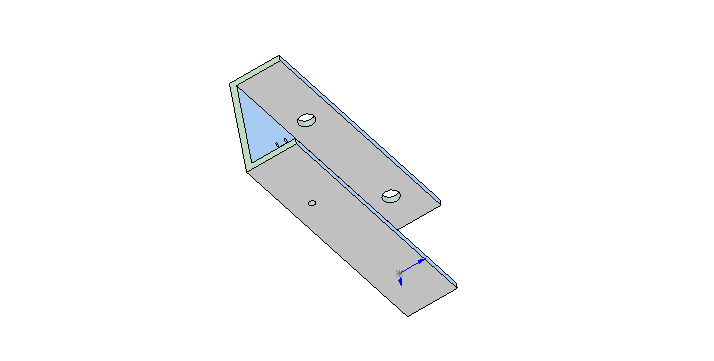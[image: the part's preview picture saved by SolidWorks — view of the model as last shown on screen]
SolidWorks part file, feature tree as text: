
SOLIDWORKS PART (.sldprt)
format: sldprt  version: not decoded by parser v0  size: 212,480 bytes
history: native  units: mm
features: sketch x4, cut_extrude x3, extrude x1 (+11 scaffold rows collapsed)
feature tree (19):
  scaffold x11  (default folders/planes/origin — collapsed)
  sketch  "Sketch1"  dims[D1=50.8mm D2=3.175mm D3=3.175mm D4=3.175mm D5=25.4mm D6=25.4mm D7=76.2mm]
  extrude  "Extrude1"  Depth=120.65mm
  sketch  "Sketch2"  dims[c1.D2=9.9822mm c1.D7=9.525mm c1.D8=2.1336mm c1.D9=9.9822mm c1.D14=4.1402mm c1.D15=4.1402mm c1.D1=25.4mm c1.D3=6.35mm c1.D4=15.7734mm c1.D5=15.875mm c1.D6=19.05mm c2.D9=8.5344mm c2.D10=4.318mm c2.D11=16.764mm c2.D12=14.732mm c2.D13=57.531mm]
  cut_extrude  "Cut-Extrude1"  [1 undecoded]
  sketch  "Sketch3"  dims[D1=3.175mm D2=9.6774mm]
  cut_extrude  "Cut-Extrude2"  [1 undecoded]
  sketch  "Sketch4"  dims[D1=7.9375mm D2=7.9375mm D3=63.5mm D4=19.05mm]
  cut_extrude  "Cut-Extrude3"  [1 undecoded]
decode coverage: 5 of 8 modeling features carry decoded parameters
note: 3 parameter values undecoded
summary: no parameter record found for 3 features
note: suppression state not decoded; provenance and decode notes live in map.json
